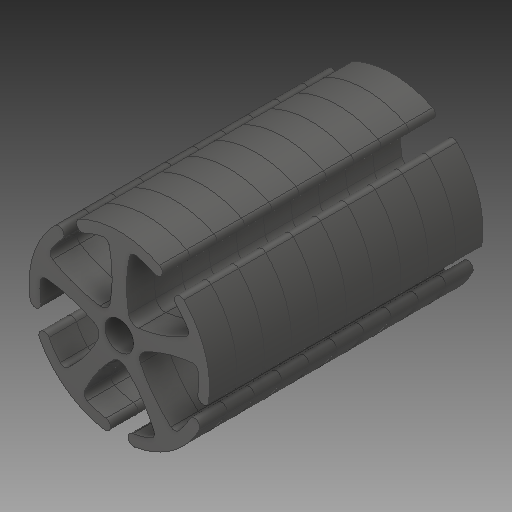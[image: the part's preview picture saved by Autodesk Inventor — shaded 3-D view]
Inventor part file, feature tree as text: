
AUTODESK INVENTOR PART (.ipt)
format: ipt  version: 2018 (Build 220112000, 112)  size: 846,336 bytes
history: native  units: in
note: dims shown in document units (in); Inventor stores cm internally (conversion verified against a paired STEP export)
features: other x9, fillet x1
ambient origin geometry x8: Origin, YZ Plane, XZ Plane, XY Plane, X Axis, Y Axis, Z Axis, Center Point
bodies: Solid1 (feature_tree), Solid2 (feature_tree), Solid3 (feature_tree), Solid4 (feature_tree), Solid5 (feature_tree), Solid6 (feature_tree), Solid7 (feature_tree), Solid8 (feature_tree), Solid9 (feature_tree), Solid10 (feature_tree)
feature tree (10):
  fillet  "Fillet1"  [1 undecoded]
  other  "LPattern1[1]"
  other  "LPattern1[2]"
  other  "LPattern1[3]"
  other  "LPattern1[4]"
  other  "LPattern1[5]"
  other  "LPattern1[6]"
  other  "LPattern1[7]"
  other  "LPattern1[8]"
  other  "LPattern1[9]"
note: 1 required parameter value undecoded (feature->parameter linkage not recoverable at this tier; creation-order binding heuristic only, values carry confidence <= 0.55)
